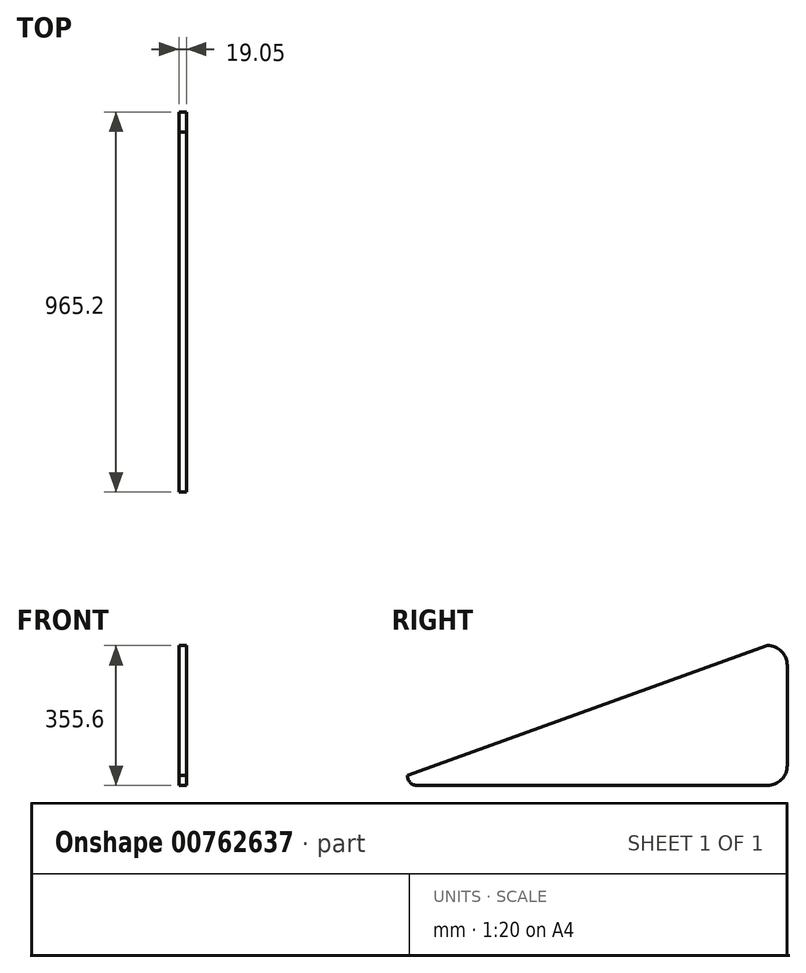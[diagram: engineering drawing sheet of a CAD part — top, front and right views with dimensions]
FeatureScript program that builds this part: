
annotation { "Feature Type Name" : "Feature", "Feature Type Description" : "" }
export const myFeature = defineFeature(function(context is Context, id is Id, definition is map)
    precondition{}
    {
        {
            var Q0;
            Q0=qCreatedBy(makeId("Right.planeOp"),FACE);
            var sketch = newSketch(context, id + "F0", { "sketchPlane" : qUnion([Q0])});
            skLineSegment(sketch, "E0.bottom", {"start": v(-482.6, 177.8) * mm, "end": v(482.6, 177.8) * mm});
            skLineSegment(sketch, "E0.top", {"start": v(-482.6, -177.8) * mm, "end": v(482.6, -177.8) * mm});
            skLineSegment(sketch, "E0.left", {"start": v(-482.6, 177.8) * mm, "end": v(-482.6, -177.8) * mm});
            skLineSegment(sketch, "E0.right", {"start": v(482.6, 177.8) * mm, "end": v(482.6, -177.8) * mm});
            skPoint(sketch, "E0.middle", {"position": v(0, 0) * mm});
            skLineSegment(sketch, "E1", {"start": v(482.6, 177.8) * mm, "end": v(431.8, 177.8) * mm});
            skLineSegment(sketch, "E2", {"start": v(431.8, 177.8) * mm, "end": v(431.8, 127) * mm});
            skLineSegment(sketch, "E3", {"start": v(482.6, -177.8) * mm, "end": v(482.6, -127) * mm});
            skLineSegment(sketch, "E4", {"start": v(482.6, -127) * mm, "end": v(431.8, -127) * mm});
            skLineSegment(sketch, "E5", {"start": v(-482.6, -177.8) * mm, "end": v(-482.6, -152.4) * mm});
            skLineSegment(sketch, "E6", {"start": v(431.8, 177.8) * mm, "end": v(-482.6, -152.4) * mm});
            skArc(sketch, "E7", {"start": v(431.8, 177.8) * mm, "mid": v(467.72, 162.92) * mm, "end": v(482.6, 127) * mm});
            skArc(sketch, "E8", {"start": v(482.6, -127) * mm, "mid": v(467.72, -162.92) * mm, "end": v(431.8, -177.8) * mm});
            skLineSegment(sketch, "E9", {"start": v(-482.6, -177.8) * mm, "end": v(-457.2, -177.8) * mm});
            skLineSegment(sketch, "E10", {"start": v(-457.2, -177.8) * mm, "end": v(-457.2, -152.4) * mm});
            skArc(sketch, "E11", {"start": v(-482.6, -152.4) * mm, "mid": v(-475.16, -170.36) * mm, "end": v(-457.2, -177.8) * mm});
            skSolve(sketch);
        }
        {
            var Q0;
            Q0=makeQuery(id+"F0.imprint","IMPRINT",FACE,{"disambiguationData":[TD([[makeQuery(id+"F0.imprint","IMPRINT",EDGE,{"derivedFrom":sQuery(id+"F0.wireOp",EDGE,"E6")}),1.0]])]});
            extrude(context, id + "F1", {"entities" : qUnion([Q0]), "depth" : 19.05 * mm, "offsetDistance" : 25.4 * mm});
        }
    });
